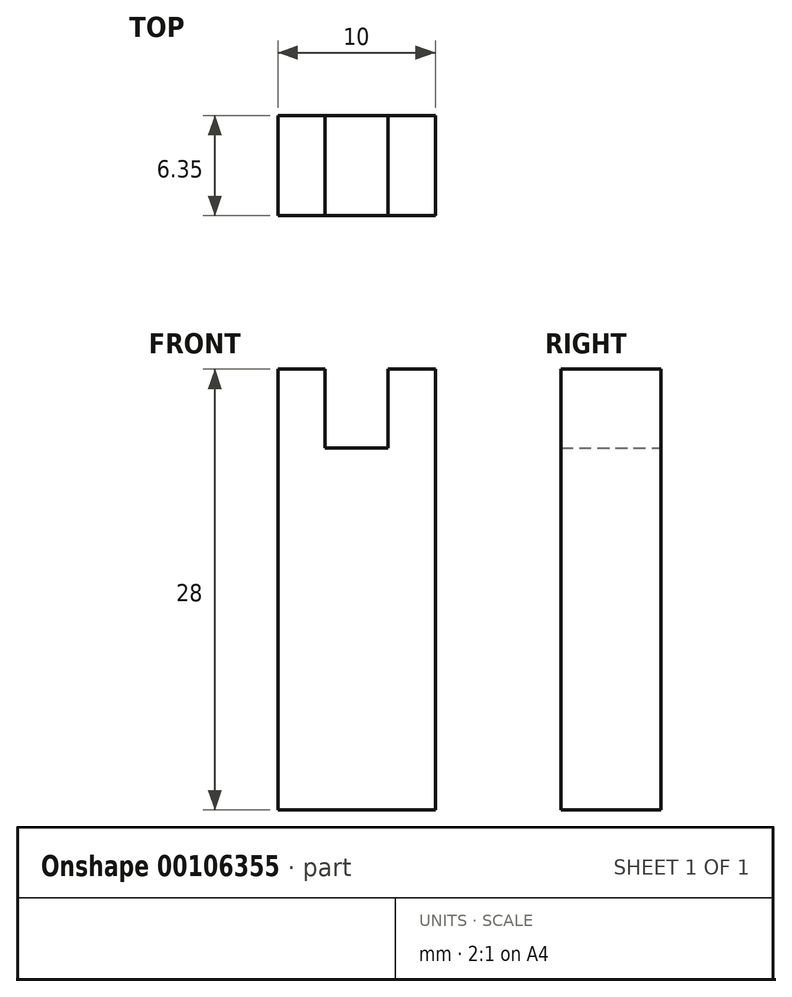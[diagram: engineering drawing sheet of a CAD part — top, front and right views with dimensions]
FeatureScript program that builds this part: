
annotation { "Feature Type Name" : "Feature", "Feature Type Description" : "" }
export const myFeature = defineFeature(function(context is Context, id is Id, definition is map)
    precondition{}
    {
        {
            var Q0;
            Q0=qCreatedBy(makeId("Front.planeOp"),FACE);
            var sketch = newSketch(context, id + "F0", { "sketchPlane" : qUnion([Q0])});
            skLineSegment(sketch, "E0", {"start": v(-5, 28) * mm, "end": v(-5, 0) * mm});
            skLineSegment(sketch, "E1", {"start": v(-5, 0) * mm, "end": v(5, 0) * mm});
            skLineSegment(sketch, "E2", {"start": v(5, 0) * mm, "end": v(5, 28) * mm});
            skLineSegment(sketch, "E3", {"start": v(5, 28) * mm, "end": v(2, 28) * mm});
            skLineSegment(sketch, "E4", {"start": v(2, 28) * mm, "end": v(2, 23) * mm});
            skLineSegment(sketch, "E5", {"start": v(2, 23) * mm, "end": v(-2, 23) * mm});
            skLineSegment(sketch, "E6", {"start": v(-2, 23) * mm, "end": v(-2, 28) * mm});
            skLineSegment(sketch, "E7", {"start": v(-2, 28) * mm, "end": v(-5, 28) * mm});
            skSolve(sketch);
        }
        {
            var Q0;
            Q0 = qSketchRegion(id + "F0", true);
            extrude(context, id + "F1", {"entities" : qUnion([Q0]), "depth" : 6.35 * mm});
        }
    });
